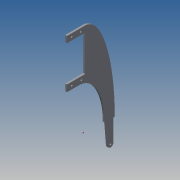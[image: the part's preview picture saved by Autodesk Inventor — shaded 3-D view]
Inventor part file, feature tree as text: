
AUTODESK INVENTOR PART (.ipt)
format: ipt  version: 2014 (Build 180170000, 170)  size: 107,520 bytes
history: native  units: mm
features: sketch x2, extrude x1
ambient origin geometry x8: Origin, YZ Plane, XZ Plane, XY Plane, X Axis, Y Axis, Z Axis, Center Point
bodies: Solid1 (feature_tree)
feature tree (3):
  sketch  "Sketch1"  dims[d10=33.5mm d11=106.0mm d12=20.5mm d13=28.5mm d15=40.5mm d16=1.5mm d17=1.5mm d18=3.5mm d19=2.0mm d20=2.0mm d21=5.5mm d22=2.0mm d23=5.5mm d24=2.0mm d25=25.0mm d26=24.5mm d27=6.5mm d28=2.0mm d29=2.0mm d30=0.0mm]
  sketch  "Sketch2"
  extrude  "Extrusion1"  Depth=2.0mm TaperAngle=0.0deg
